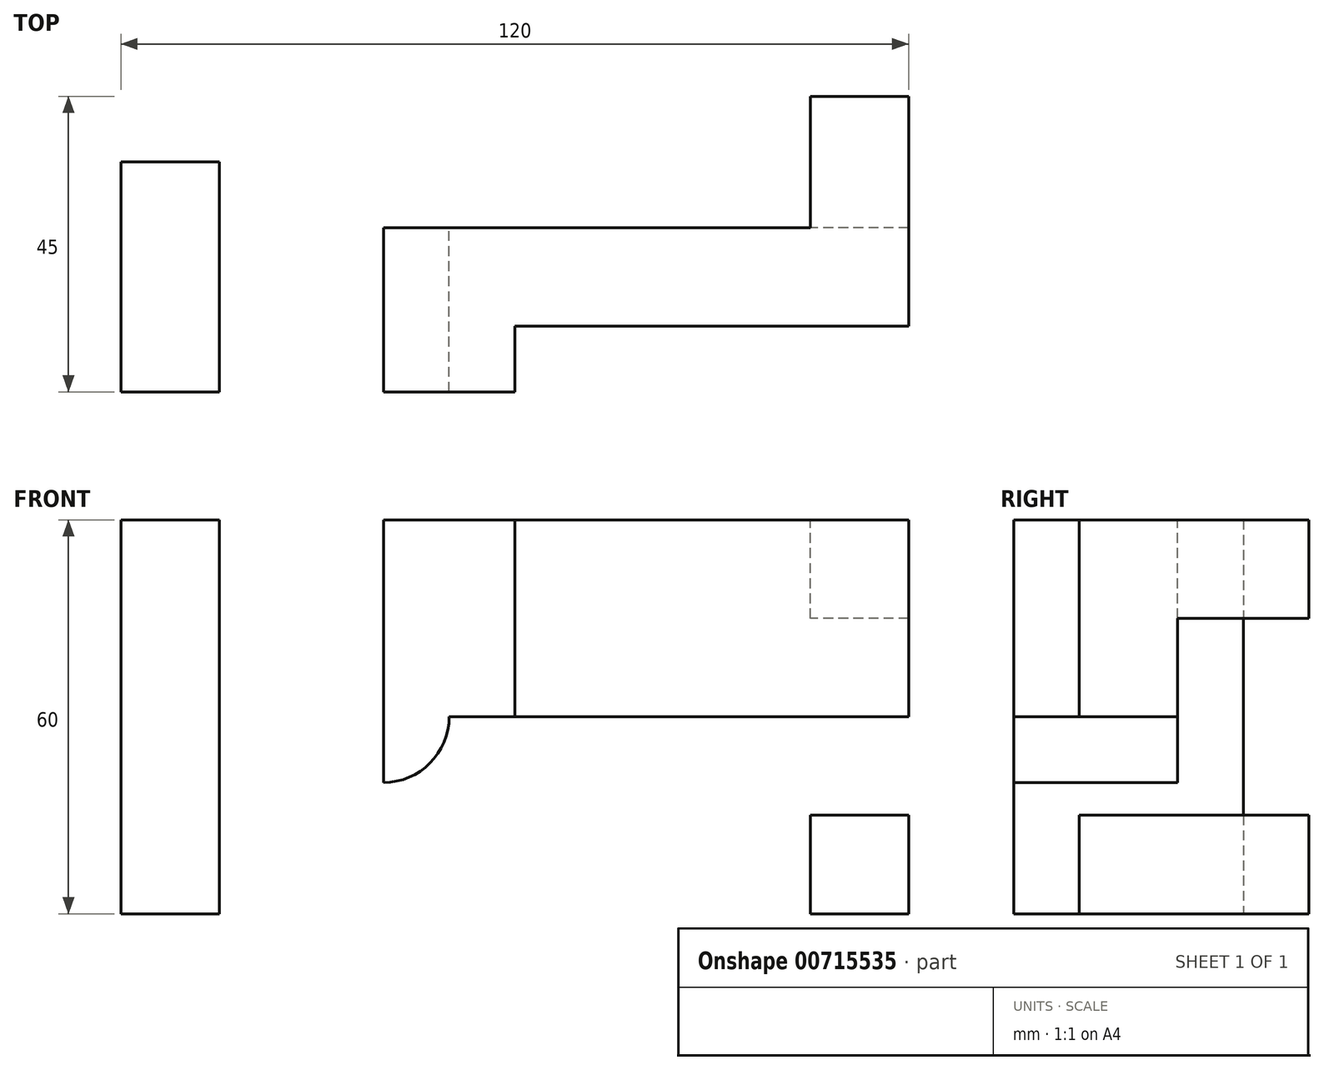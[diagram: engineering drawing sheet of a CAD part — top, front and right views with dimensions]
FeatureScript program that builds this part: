
annotation { "Feature Type Name" : "Feature", "Feature Type Description" : "" }
export const myFeature = defineFeature(function(context is Context, id is Id, definition is map)
    precondition{}
    {
        {
            var Q0;
            Q0=qCreatedBy(makeId("Top.planeOp"),FACE);
            var sketch = newSketch(context, id + "F0", { "sketchPlane" : qUnion([Q0])});
            skLineSegment(sketch, "E0", {"start": v(-54.4, 18.98) * mm, "end": v(-54.4, -16.02) * mm});
            skLineSegment(sketch, "E1", {"start": v(-54.4, -16.02) * mm, "end": v(5.6, -16.02) * mm});
            skLineSegment(sketch, "E2", {"start": v(5.6, -16.02) * mm, "end": v(5.6, -6.02) * mm});
            skLineSegment(sketch, "E3", {"start": v(5.6, -6.02) * mm, "end": v(65.6, -6.02) * mm});
            skLineSegment(sketch, "E4", {"start": v(65.6, -6.02) * mm, "end": v(65.6, 28.98) * mm});
            skLineSegment(sketch, "E5", {"start": v(65.6, 28.98) * mm, "end": v(50.6, 28.98) * mm});
            skLineSegment(sketch, "E6", {"start": v(50.6, 28.98) * mm, "end": v(50.6, 8.98) * mm});
            skLineSegment(sketch, "E7", {"start": v(50.6, 8.98) * mm, "end": v(-39.4, 8.98) * mm});
            skLineSegment(sketch, "E8", {"start": v(-39.4, 8.98) * mm, "end": v(-39.4, 18.98) * mm});
            skLineSegment(sketch, "E9", {"start": v(-39.4, 18.98) * mm, "end": v(-54.4, 18.98) * mm});
            skLineSegment(sketch, "E10", {"start": v(50.6, 8.98) * mm, "end": v(65.6, 8.98) * mm});
            skSolve(sketch);
        }
        {
            var Q0;
            Q0=makeQuery(id+"F0.imprint","IMPRINT",FACE,{"disambiguationData":[TD([[makeQuery(id+"F0.imprint","IMPRINT",EDGE,{"derivedFrom":sQuery(id+"F0.wireOp",EDGE,"E0")}),1.0]])]});
            extrude(context, id + "F1", {"entities" : qUnion([Q0]), "depth" : 30 * mm, "offsetDistance" : 25 * mm});
        }
        {
            var Q0;
            Q0 = qSketchRegion(id + "F0", true);
            extrude(context, id + "F2", {"entities" : qUnion([Q0]), "operationType" : NewBodyOperationType.ADD, "depth" : 15 * mm, "offsetDistance" : 25 * mm});
        }
        {
            var Q0;
            Q0=makeQuery(id+"F1.opExtrude","SWEPT_BODY",BODY,{"disambiguationData":[OSD([sQuery(id+"F0.wireOp",EDGE,"E0"),sQuery(id+"F0.wireOp",EDGE,"E1"),sQuery(id+"F0.wireOp",EDGE,"E2"),sQuery(id+"F0.wireOp",EDGE,"E3"),sQuery(id+"F0.wireOp",EDGE,"E4"),sQuery(id+"F0.wireOp",EDGE,"E7"),sQuery(id+"F0.wireOp",EDGE,"E8"),sQuery(id+"F0.wireOp",EDGE,"E9"),sQuery(id+"F0.wireOp",EDGE,"E10")])]});
            var Q1;
            Q1=makeQuery(id+"F1.opExtrude","CAP_FACE",FACE,{"disambiguationData":[OSD([sQuery(id+"F0.wireOp",EDGE,"E0"),sQuery(id+"F0.wireOp",EDGE,"E1"),sQuery(id+"F0.wireOp",EDGE,"E2"),sQuery(id+"F0.wireOp",EDGE,"E3"),sQuery(id+"F0.wireOp",EDGE,"E4"),sQuery(id+"F0.wireOp",EDGE,"E7"),sQuery(id+"F0.wireOp",EDGE,"E8"),sQuery(id+"F0.wireOp",EDGE,"E9"),sQuery(id+"F0.wireOp",EDGE,"E10")])],"isStart":false});
            mirror(context, id + "F3", {"operationType" : NewBodyOperationType.ADD, "entities" : qUnion([Q0]), "mirrorPlane" : qUnion([Q1])});
        }
        {
            var Q0;
            {var subQ0=makeQuery(id+"F1.opExtrude","SWEPT_FACE",FACE,{"disambiguationData":[OSD([sQuery(id+"F0.wireOp",EDGE,"E7"),sQuery(id+"F0.wireOp",EDGE,"E10")])]});Q0=makeQuery(id+"F3.boolean.opBoolean","MERGE",FACE,{"derivedFrom":[subQ0,makeQuery(id+"F3.opPattern","COPY",FACE,{"derivedFrom":subQ0,"instanceName":"1"})]});}
            var sketch = newSketch(context, id + "F4", { "sketchPlane" : qUnion([Q0])});
            skLineSegment(sketch, "E11", {"start": v(-50.6, 60) * mm, "end": v(-30.6, 60) * mm});
            skLineSegment(sketch, "E12", {"start": v(-30.6, 60) * mm, "end": v(-30.6, 0) * mm});
            skLineSegment(sketch, "E13", {"start": v(-65.6, 45) * mm, "end": v(-65.6, 30) * mm});
            skLineSegment(sketch, "E14", {"start": v(-65.6, 30) * mm, "end": v(39.4, 30) * mm});
            skPoint(sketch, "E15", {"position": v(-30.6, 30) * mm});
            skCircle(sketch, "E16", {"center": v(-30.6, 30) * mm, "radius": 10 * mm});
            skLineSegment(sketch, "E17", {"start": v(-30.6, 60) * mm, "end": v(14.4, 60) * mm});
            skLineSegment(sketch, "E18", {"start": v(14.4, 60) * mm, "end": v(14.4, 0) * mm});
            skPoint(sketch, "E19", {"position": v(14.4, 30) * mm});
            skCircle(sketch, "E20", {"center": v(14.4, 30) * mm, "radius": 10 * mm});
            skSolve(sketch);
        }
        {
            var Q0;
            {var subQ0=sQuery(id+"F4.wireOp",EDGE,"E14");var subQ1=sQuery(id+"F4.wireOp",EDGE,"E12");var subQ2=makeQuery(id+"F4.imprint","INTERSECT",VERTEX,{"derivedFrom":[subQ1,subQ0]});Q0=makeQuery(id+"F4.imprint","IMPRINT",FACE,{"disambiguationData":[TD([[makeQuery(id+"F4.imprint","IMPRINT",EDGE,{"disambiguationData":[TD([[subQ2,-1.0]])],"derivedFrom":subQ1}),-1.0]])]});}
            var Q1;
            {var subQ0=sQuery(id+"F4.wireOp",EDGE,"E14");var subQ1=sQuery(id+"F4.wireOp",EDGE,"E12");var subQ2=makeQuery(id+"F4.imprint","INTERSECT",VERTEX,{"derivedFrom":[subQ1,subQ0]});Q1=makeQuery(id+"F4.imprint","IMPRINT",FACE,{"disambiguationData":[TD([[makeQuery(id+"F4.imprint","IMPRINT",EDGE,{"disambiguationData":[TD([[subQ2,-1.0]])],"derivedFrom":subQ1}),1.0]])]});}
            var Q2;
            {var subQ0=sQuery(id+"F4.wireOp",EDGE,"E16");var subQ1=sQuery(id+"F4.wireOp",EDGE,"E12");var subQ2=makeQuery(id+"F4.imprint","INTERSECT",VERTEX,{"disambiguationData":[OD(0.0)],"derivedFrom":[subQ1,subQ0]});Q2=makeQuery(id+"F4.imprint","IMPRINT",FACE,{"disambiguationData":[TD([[makeQuery(id+"F4.imprint","IMPRINT",EDGE,{"disambiguationData":[TD([[subQ2,-1.0]])],"derivedFrom":subQ1}),1.0]])]});}
            var Q3;
            {var subQ0=sQuery(id+"F4.wireOp",EDGE,"E16");var subQ1=sQuery(id+"F4.wireOp",EDGE,"E12");var subQ2=makeQuery(id+"F4.imprint","INTERSECT",VERTEX,{"disambiguationData":[OD(0.0)],"derivedFrom":[subQ1,subQ0]});Q3=makeQuery(id+"F4.imprint","IMPRINT",FACE,{"disambiguationData":[TD([[makeQuery(id+"F4.imprint","IMPRINT",EDGE,{"disambiguationData":[TD([[subQ2,-1.0]])],"derivedFrom":subQ1}),-1.0]])]});}
            var Q4;
            {var subQ0=sQuery(id+"F4.wireOp",EDGE,"E18");var subQ1=sQuery(id+"F4.wireOp",EDGE,"E14");var subQ2=makeQuery(id+"F4.imprint","INTERSECT",VERTEX,{"derivedFrom":[subQ1,subQ0]});Q4=makeQuery(id+"F4.imprint","IMPRINT",FACE,{"disambiguationData":[TD([[makeQuery(id+"F4.imprint","IMPRINT",EDGE,{"disambiguationData":[TD([[subQ2,-1.0]])],"derivedFrom":subQ1}),-1.0]])]});}
            var Q5;
            {var subQ0=sQuery(id+"F4.wireOp",EDGE,"E20");var subQ1=sQuery(id+"F4.wireOp",EDGE,"E14");var subQ2=makeQuery(id+"F4.imprint","INTERSECT",VERTEX,{"disambiguationData":[OD(0.0)],"derivedFrom":[subQ1,subQ0]});Q5=makeQuery(id+"F4.imprint","IMPRINT",FACE,{"disambiguationData":[TD([[makeQuery(id+"F4.imprint","IMPRINT",EDGE,{"disambiguationData":[TD([[subQ2,-1.0]])],"derivedFrom":subQ1}),-1.0]])]});}
            var Q6;
            {var subQ0=sQuery(id+"F4.wireOp",EDGE,"E20");var subQ1=sQuery(id+"F4.wireOp",EDGE,"E14");var subQ2=makeQuery(id+"F4.imprint","INTERSECT",VERTEX,{"disambiguationData":[OD(0.0)],"derivedFrom":[subQ1,subQ0]});Q6=makeQuery(id+"F4.imprint","IMPRINT",FACE,{"disambiguationData":[TD([[makeQuery(id+"F4.imprint","IMPRINT",EDGE,{"disambiguationData":[TD([[subQ2,-1.0]])],"derivedFrom":subQ1}),1.0]])]});}
            var Q7;
            {var subQ0=sQuery(id+"F4.wireOp",EDGE,"E18");var subQ1=sQuery(id+"F4.wireOp",EDGE,"E14");var subQ2=makeQuery(id+"F4.imprint","INTERSECT",VERTEX,{"derivedFrom":[subQ1,subQ0]});Q7=makeQuery(id+"F4.imprint","IMPRINT",FACE,{"disambiguationData":[TD([[makeQuery(id+"F4.imprint","IMPRINT",EDGE,{"disambiguationData":[TD([[subQ2,-1.0]])],"derivedFrom":subQ1}),1.0]])]});}
            extrude(context, id + "F5", {"entities" : qUnion([Q0, Q1, Q2, Q3, Q4, Q5, Q6, Q7]), "operationType" : NewBodyOperationType.REMOVE, "endBound" : BoundingType.THROUGH_ALL, "oppositeDirection" : true, "depth" : 25 * mm, "offsetDistance" : 25 * mm});
        }
    });
